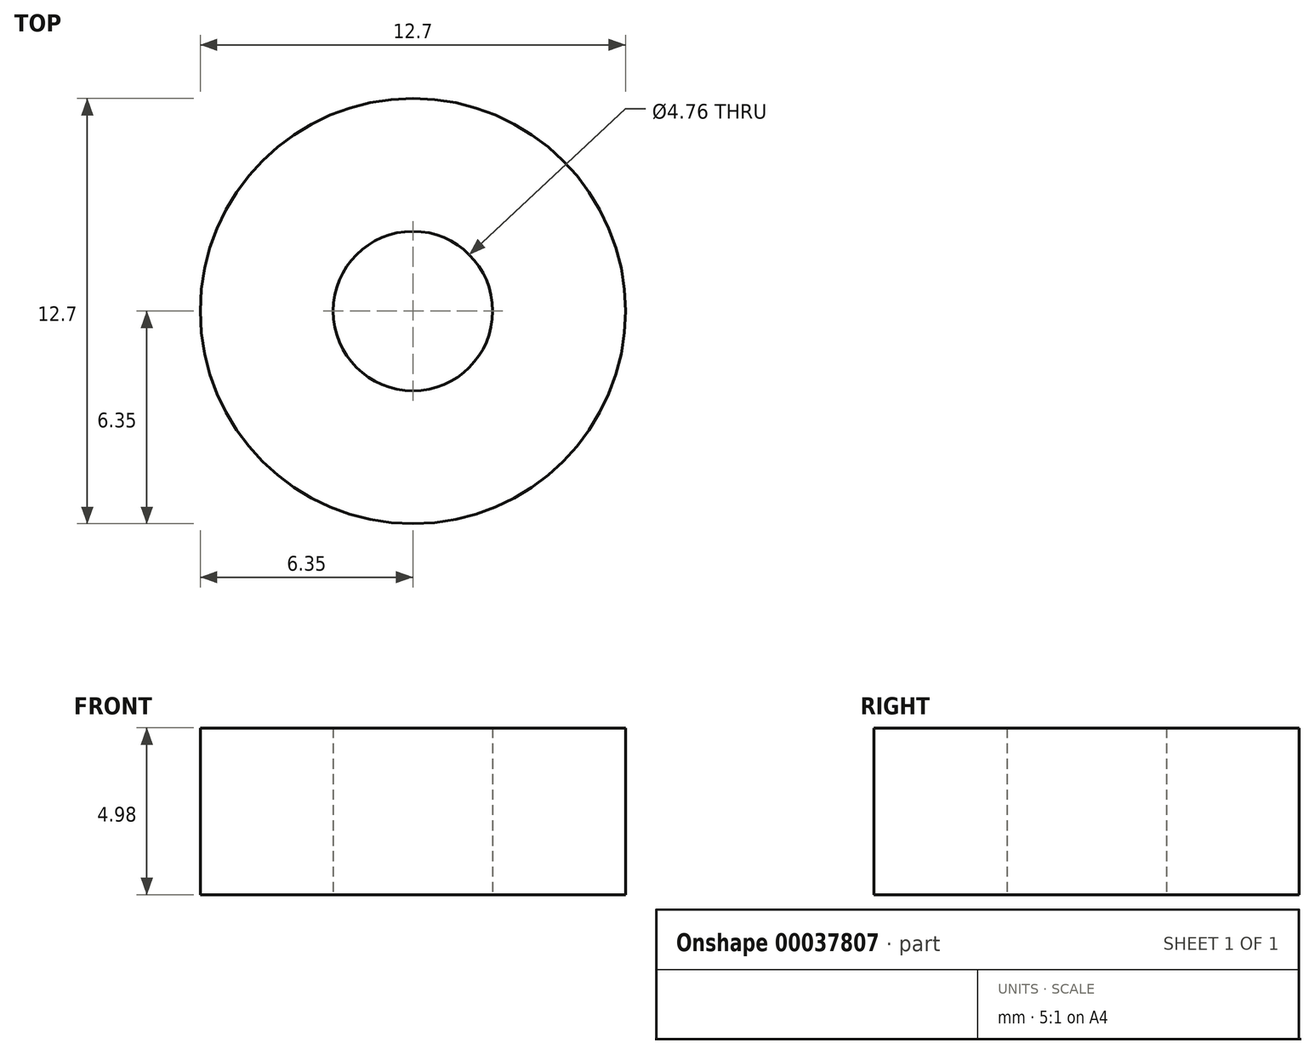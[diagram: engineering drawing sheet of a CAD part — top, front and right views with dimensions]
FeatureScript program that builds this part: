
annotation { "Feature Type Name" : "Feature", "Feature Type Description" : "" }
export const myFeature = defineFeature(function(context is Context, id is Id, definition is map)
    precondition{}
    {
        {
            var Q0;
            Q0=qCreatedBy(makeId("Top.planeOp"),FACE);
            var sketch = newSketch(context, id + "F0", { "sketchPlane" : qUnion([Q0])});
            skCircle(sketch, "E0", {"center": v(0, 0) * mm, "radius": 6.35 * mm});
            skCircle(sketch, "E1", {"center": v(0, 0) * mm, "radius": 2.38 * mm});
            skSolve(sketch);
        }
        {
            var Q0;
            Q0 = qSketchRegion(id + "F0", true);
            extrude(context, id + "F1", {"entities" : qUnion([Q0]), "depth" : 4.98 * mm});
        }
    });
